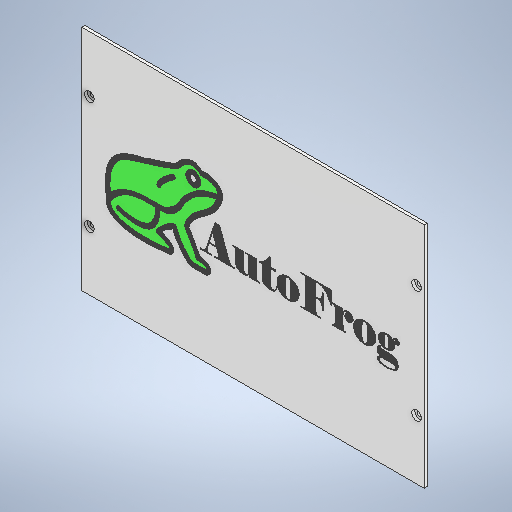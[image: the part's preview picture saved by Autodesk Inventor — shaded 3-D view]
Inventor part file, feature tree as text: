
AUTODESK INVENTOR PART (.ipt)
format: ipt  version: 2025 (Build 290162000, 162)  size: 1,322,496 bytes
history: native  units: in
note: dims shown in document units (in); Inventor stores cm internally (conversion verified against a paired STEP export)
features: projected_geometry x22, extrude x9, sketch x9, other x5, reference x3
ambient origin geometry x8: Origin, YZ Plane, XZ Plane, XY Plane, X Axis, Y Axis, Z Axis, Center Point
bodies: Solid1 (feature_tree), Solid2 (feature_tree), Solid3 (feature_tree)
feature tree (48):
  extrude  "Extrusion1"  Depth=8.8425in
  extrude  "Extrusion2"  Depth=0.0787in
  extrude  "Extrusion3"  Depth=0.0394in
  extrude  "Extrusion4"  Depth=0.0394in
  extrude  "Extrusion5"  Depth=0.0787in TaperAngle=0.0deg
  extrude  "Extrusion6"  Depth=0.126in
  extrude  "Extrusion7"  Depth=0.126in
  extrude  "Extrusion8"  Depth=4.3333in
  extrude  "Extrusion9"  Depth=0.0394in TaperAngle=0.0deg
  sketch  "Sketch1"  dims[d0=0.0787in d1=8.8425in]
  reference  "Reference1"
  sketch  "Sketch2"  dims[d2=0.0787in d3=0.0in d4=0.0787in]
  projected_geometry  "Projected Loop1"
  sketch  "Sketch4"  dims[d5=0.0787in d6=0.0in d7=0.0394in]
  reference  "Reference2"
  reference  "Reference3"
  sketch  "Sketch5"  dims[d8=0.0394in d9=0.0394in]
  projected_geometry  "Projected Loop2"
  projected_geometry  "Projected Loop3"
  projected_geometry  "Projected Loop4"
  projected_geometry  "Projected Loop5"
  sketch  "Sketch6"  dims[d10=0.0394in d11=0.0787in d12=0.0in]
  other  "Image1"
  projected_geometry  "Projected Loop6"
  sketch  "Sketch7"  dims[d13=0.126in d14=0.126in]
  sketch  "Sketch8"  dims[d15=0.126in d16=0.126in]
  projected_geometry  "Projected Loop7"
  projected_geometry  "Projected Loop8"
  projected_geometry  "Projected Loop9"
  projected_geometry  "Projected Loop10"
  projected_geometry  "Projected Loop11"
  projected_geometry  "Projected Loop12"
  projected_geometry  "Projected Loop13"
  projected_geometry  "Projected Loop14"
  projected_geometry  "Projected Loop15"
  projected_geometry  "Projected Loop16"
  projected_geometry  "Projected Loop17"
  sketch  "Sketch9"  dims[d17=0.0787in d18=0.0in d35=4.3333in]
  projected_geometry  "Projected Loop18"
  projected_geometry  "Projected Loop19"
  sketch  "Sketch10"  dims[d56=0.0394in d57=0.0in d58=0.0394in d59=0.0in d60=0.0394in d61=0.0in d62=0.0394in d63=0.0in d64=0.0394in d65=0.0in]
  projected_geometry  "Projected Loop20"
  projected_geometry  "Projected Loop21"
  projected_geometry  "Projected Loop22"
  other  "<userpath>\Documents\GitHub\AutoFrog2\CAD\truefit.iam"
  other  "truefit.iam"
  other  "rightwall:1"
  other  "leftwall:1"
